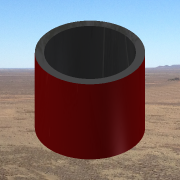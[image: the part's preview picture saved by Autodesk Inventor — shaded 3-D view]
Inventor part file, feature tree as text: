
AUTODESK INVENTOR PART (.ipt)
format: ipt  version: 2014 SP1 (Build 180222100, 222)  size: 127,488 bytes
history: native  units: in
note: dims shown in document units (in); Inventor stores cm internally (conversion verified against a paired STEP export)
features: extrude x1, sketch x1
ambient origin geometry x8: Origin, YZ Plane, XZ Plane, XY Plane, X Axis, Y Axis, Z Axis, Center Point
bodies: Solid1 (feature_tree)
feature tree (2):
  extrude  "Extrusion1"  Depth=1.0in TaperAngle=0.0deg
  sketch  "Sketch1"  dims[d0=1.0in d1=1.0in d2=0.0in d3=0.1in]
